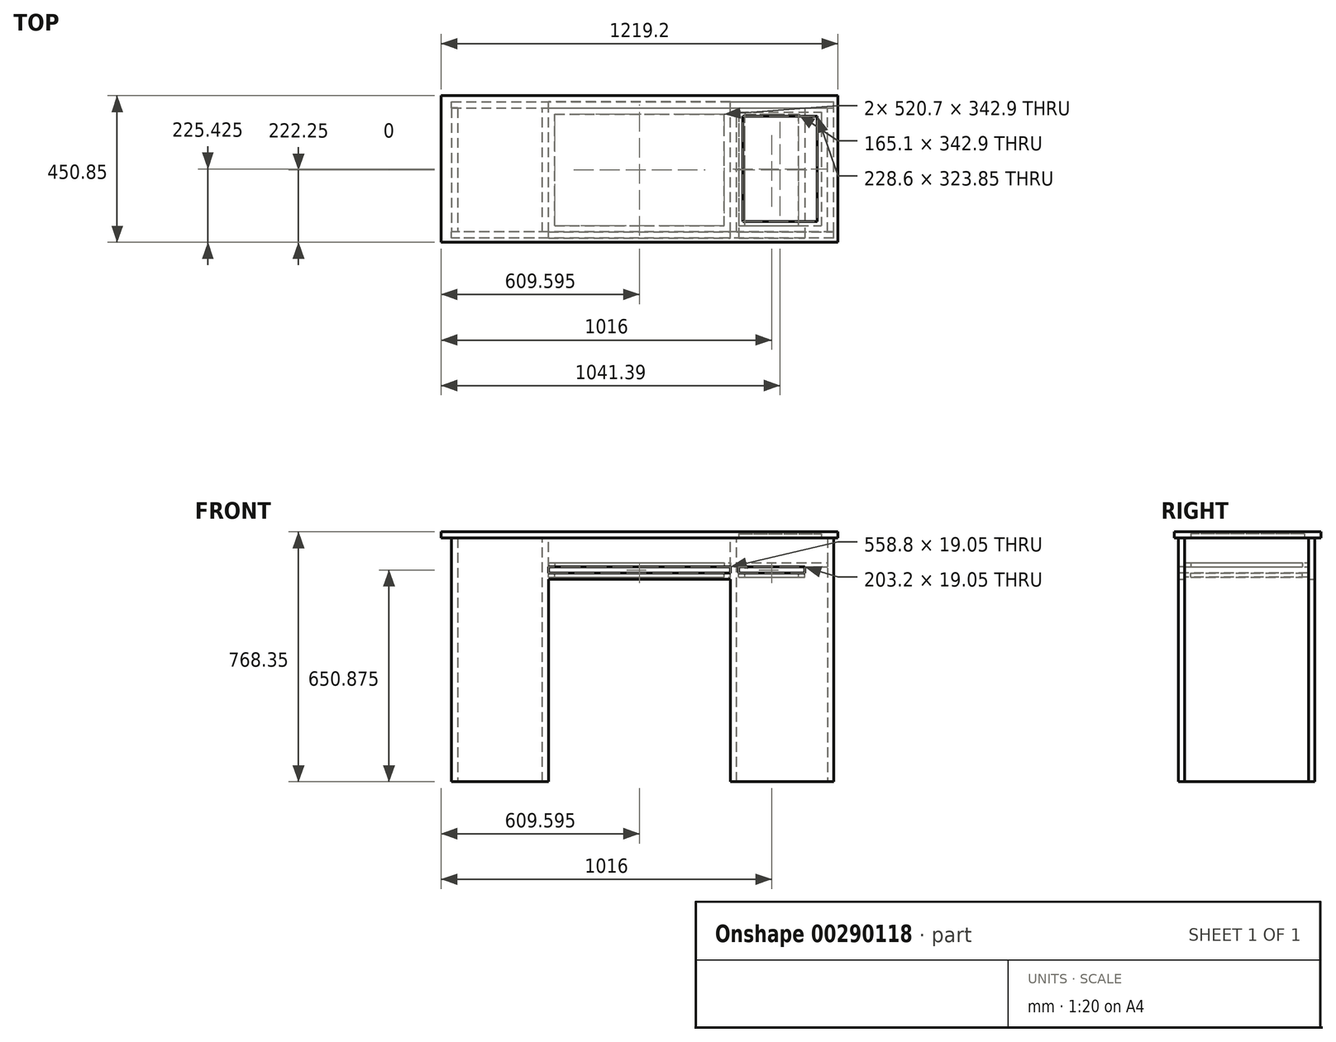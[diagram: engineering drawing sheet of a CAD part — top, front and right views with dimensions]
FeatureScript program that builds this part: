
annotation { "Feature Type Name" : "Feature", "Feature Type Description" : "" }
export const myFeature = defineFeature(function(context is Context, id is Id, definition is map)
    precondition{}
    {
        {
            var Q0;
            Q0=qCreatedBy(makeId("Front.planeOp"),FACE);
            var sketch = newSketch(context, id + "F0", { "sketchPlane" : qUnion([Q0])});
            skLineSegment(sketch, "E0.bottom", {"start": v(587.37, 374.65) * mm, "end": v(-587.38, 374.65) * mm});
            skLineSegment(sketch, "E0.top", {"start": v(587.38, -374.65) * mm, "end": v(269.87, -374.65) * mm});
            skLineSegment(sketch, "E0.left", {"start": v(587.38, 374.65) * mm, "end": v(587.38, -374.65) * mm});
            skLineSegment(sketch, "E0.right", {"start": v(-587.38, 374.65) * mm, "end": v(-587.38, -374.65) * mm});
            skPoint(sketch, "E0.middle", {"position": v(0, 0) * mm});
            skLineSegment(sketch, "E1", {"start": v(-288.93, -374.65) * mm, "end": v(-288.93, 247.65) * mm});
            skLineSegment(sketch, "E2", {"start": v(-288.93, 247.65) * mm, "end": v(269.87, 247.65) * mm});
            skLineSegment(sketch, "E3", {"start": v(269.87, 247.65) * mm, "end": v(269.87, -374.65) * mm});
            skLineSegment(sketch, "E4.trimOffspring", {"start": v(-288.93, -374.65) * mm, "end": v(-587.37, -374.65) * mm});
            skSolve(sketch);
        }
        {
            var Q0;
            Q0 = qSketchRegion(id + "F0", true);
            extrude(context, id + "F1", {"entities" : qUnion([Q0]), "depth" : 19.05 * mm});
        }
        {
            var Q0;
            Q0=makeQuery(id+"F1.opExtrude","SWEPT_FACE",FACE,{"disambiguationData":[OSD([sQuery(id+"F0.wireOp",EDGE,"E0.bottom")])]});
            var sketch = newSketch(context, id + "F2", { "sketchPlane" : qUnion([Q0])});
            skLineSegment(sketch, "E5.bottom", {"start": v(-619.13, -31.75) * mm, "end": v(600.07, -31.75) * mm});
            skLineSegment(sketch, "E5.top", {"start": v(-619.13, 419.1) * mm, "end": v(600.07, 419.1) * mm});
            skLineSegment(sketch, "E5.left", {"start": v(-619.13, -31.75) * mm, "end": v(-619.13, 419.1) * mm});
            skLineSegment(sketch, "E5.right", {"start": v(600.07, -31.75) * mm, "end": v(600.07, 419.1) * mm});
            skSolve(sketch);
        }
        {
            var Q0;
            Q0 = qSketchRegion(id + "F2", true);
            extrude(context, id + "F3", {"entities" : qUnion([Q0]), "operationType" : NewBodyOperationType.ADD, "depth" : 19.05 * mm});
        }
        {
            var Q0;
            Q0=qCreatedBy(makeId("Front.planeOp"),FACE);
            cPlane(context, id + "F4", {"entities" : qUnion([Q0]), "cplaneType" : CPlaneType.OFFSET, "offset" : 400.05 * mm, "oppositeDirection" : true, "width" : 152.4 * mm, "height" : 152.4 * mm});
        }
        {
            var Q0;
            Q0=qCreatedBy(id+"F4.planeOp",FACE);
            var sketch = newSketch(context, id + "F5", { "sketchPlane" : qUnion([Q0])});
            skLineSegment(sketch, "E6.bottom", {"start": v(-587.38, 374.65) * mm, "end": v(587.38, 374.65) * mm});
            skLineSegment(sketch, "E6.top", {"start": v(-587.38, -374.65) * mm, "end": v(-288.93, -374.65) * mm});
            skLineSegment(sketch, "E6.left", {"start": v(-587.38, 374.65) * mm, "end": v(-587.38, -374.65) * mm});
            skLineSegment(sketch, "E6.right", {"start": v(587.38, 374.65) * mm, "end": v(587.38, -374.65) * mm});
            skPoint(sketch, "E6.middle", {"position": v(0, 0) * mm});
            skLineSegment(sketch, "E7", {"start": v(269.87, -374.65) * mm, "end": v(269.87, 247.65) * mm});
            skLineSegment(sketch, "E8", {"start": v(269.87, 247.65) * mm, "end": v(-288.93, 247.65) * mm});
            skLineSegment(sketch, "E9", {"start": v(-288.93, 247.65) * mm, "end": v(-288.93, -374.65) * mm});
            skLineSegment(sketch, "E10.trimOffspring", {"start": v(269.87, -374.65) * mm, "end": v(587.38, -374.65) * mm});
            skSolve(sketch);
        }
        {
            var Q0;
            Q0 = qSketchRegion(id + "F5", true);
            extrude(context, id + "F6", {"entities" : qUnion([Q0]), "operationType" : NewBodyOperationType.ADD, "depth" : 19.05 * mm});
        }
        {
            var Q0;
            Q0=qCreatedBy(makeId("Right.planeOp"),FACE);
            cPlane(context, id + "F7", {"entities" : qUnion([Q0]), "cplaneType" : CPlaneType.OFFSET, "offset" : 587.68 * mm, "width" : 152.4 * mm, "height" : 152.4 * mm});
        }
        {
            var Q0;
            Q0=qCreatedBy(makeId("Right.planeOp"),FACE);
            cPlane(context, id + "F8", {"entities" : qUnion([Q0]), "cplaneType" : CPlaneType.OFFSET, "offset" : 587.68 * mm, "oppositeDirection" : true, "width" : 152.4 * mm, "height" : 152.4 * mm});
        }
        {
            var Q0;
            Q0=qCreatedBy(id+"F8.planeOp",FACE);
            var sketch = newSketch(context, id + "F9", { "sketchPlane" : qUnion([Q0])});
            skLineSegment(sketch, "E11.bottom", {"start": v(381, 374.65) * mm, "end": v(0, 374.65) * mm});
            skLineSegment(sketch, "E11.top", {"start": v(381, -374.65) * mm, "end": v(0, -374.65) * mm});
            skLineSegment(sketch, "E11.left", {"start": v(381, 374.65) * mm, "end": v(381, -374.65) * mm});
            skLineSegment(sketch, "E11.right", {"start": v(0, 374.65) * mm, "end": v(0, -374.65) * mm});
            skSolve(sketch);
        }
        {
            var Q0;
            Q0=makeQuery(id+"F9.imprint","IMPRINT",FACE,{"disambiguationData":[TD([[makeQuery(id+"F9.imprint","IMPRINT",EDGE,{"derivedFrom":sQuery(id+"F9.wireOp",EDGE,"E11.bottom")}),1.0]])]});
            extrude(context, id + "F10", {"entities" : qUnion([Q0]), "depth" : 19.05 * mm});
        }
        {
            var Q0;
            Q0=qCreatedBy(id+"F7.planeOp",FACE);
            var sketch = newSketch(context, id + "F11", { "sketchPlane" : qUnion([Q0])});
            skLineSegment(sketch, "E12.bottom", {"start": v(0, 374.65) * mm, "end": v(381, 374.65) * mm});
            skLineSegment(sketch, "E12.top", {"start": v(0, -374.65) * mm, "end": v(381, -374.65) * mm});
            skLineSegment(sketch, "E12.left", {"start": v(0, 374.65) * mm, "end": v(0, -374.65) * mm});
            skLineSegment(sketch, "E12.right", {"start": v(381, 374.65) * mm, "end": v(381, -374.65) * mm});
            skSolve(sketch);
        }
        {
            var Q0;
            Q0 = qSketchRegion(id + "F11", true);
            extrude(context, id + "F12", {"entities" : qUnion([Q0]), "oppositeDirection" : true, "depth" : 19.05 * mm});
        }
        {
            var Q0;
            Q0=makeQuery(id+"F1.opExtrude","CAP_FACE",FACE,{"disambiguationData":[OSD([sQuery(id+"F0.wireOp",EDGE,"E0.bottom"),sQuery(id+"F0.wireOp",EDGE,"E0.top"),sQuery(id+"F0.wireOp",EDGE,"E0.left"),sQuery(id+"F0.wireOp",EDGE,"E0.right"),sQuery(id+"F0.wireOp",EDGE,"E1"),sQuery(id+"F0.wireOp",EDGE,"E2"),sQuery(id+"F0.wireOp",EDGE,"E3"),sQuery(id+"F0.wireOp",EDGE,"E4.trimOffspring")])],"isStart":false});
            var sketch = newSketch(context, id + "F13", { "sketchPlane" : qUnion([Q0])});
            skLineSegment(sketch, "E13.bottom", {"start": v(-288.93, 285.75) * mm, "end": v(269.88, 285.75) * mm});
            skLineSegment(sketch, "E13.top", {"start": v(-288.93, 266.7) * mm, "end": v(269.88, 266.7) * mm});
            skLineSegment(sketch, "E13.left", {"start": v(-288.93, 285.75) * mm, "end": v(-288.93, 266.7) * mm});
            skLineSegment(sketch, "E13.right", {"start": v(269.88, 285.75) * mm, "end": v(269.88, 266.7) * mm});
            skSolve(sketch);
        }
        {
            var Q0;
            Q0=makeQuery(id+"F13.imprint","IMPRINT",FACE,{"disambiguationData":[TD([[makeQuery(id+"F13.imprint","IMPRINT",EDGE,{"derivedFrom":sQuery(id+"F13.wireOp",EDGE,"E13.bottom")}),-1.0]])]});
            extrude(context, id + "F14", {"entities" : qUnion([Q0]), "operationType" : NewBodyOperationType.REMOVE, "oppositeDirection" : true, "depth" : 19.05 * mm});
        }
        {
            var Q0;
            Q0=makeQuery(id+"F1.opExtrude","CAP_FACE",FACE,{"disambiguationData":[OSD([sQuery(id+"F0.wireOp",EDGE,"E0.bottom"),sQuery(id+"F0.wireOp",EDGE,"E0.top"),sQuery(id+"F0.wireOp",EDGE,"E0.left"),sQuery(id+"F0.wireOp",EDGE,"E0.right"),sQuery(id+"F0.wireOp",EDGE,"E1"),sQuery(id+"F0.wireOp",EDGE,"E2"),sQuery(id+"F0.wireOp",EDGE,"E3"),sQuery(id+"F0.wireOp",EDGE,"E4.trimOffspring")])],"isStart":false});
            var sketch = newSketch(context, id + "F15", { "sketchPlane" : qUnion([Q0])});
            skLineSegment(sketch, "E14.bottom", {"start": v(295.28, 266.7) * mm, "end": v(498.48, 266.7) * mm});
            skLineSegment(sketch, "E14.top", {"start": v(295.28, 285.75) * mm, "end": v(498.48, 285.75) * mm});
            skLineSegment(sketch, "E14.left", {"start": v(295.28, 266.7) * mm, "end": v(295.28, 285.75) * mm});
            skLineSegment(sketch, "E14.right", {"start": v(498.48, 266.7) * mm, "end": v(498.48, 285.75) * mm});
            skSolve(sketch);
        }
        {
            var Q0;
            Q0=makeQuery(id+"F15.imprint","IMPRINT",FACE,{"disambiguationData":[TD([[makeQuery(id+"F15.imprint","IMPRINT",EDGE,{"derivedFrom":sQuery(id+"F15.wireOp",EDGE,"E14.bottom")}),1.0]])]});
            extrude(context, id + "F16", {"entities" : qUnion([Q0]), "operationType" : NewBodyOperationType.REMOVE, "oppositeDirection" : true, "depth" : 19.05 * mm});
        }
        {
            var Q0;
            Q0=makeQuery(id+"F3.opExtrude","CAP_FACE",FACE,{"disambiguationData":[OSD([sQuery(id+"F2.wireOp",EDGE,"E5.bottom"),sQuery(id+"F2.wireOp",EDGE,"E5.top"),sQuery(id+"F2.wireOp",EDGE,"E5.left"),sQuery(id+"F2.wireOp",EDGE,"E5.right")])],"isStart":false});
            var sketch = newSketch(context, id + "F17", { "sketchPlane" : qUnion([Q0])});
            skLineSegment(sketch, "E15.bottom", {"start": v(307.97, 355.6) * mm, "end": v(536.57, 355.6) * mm});
            skLineSegment(sketch, "E15.top", {"start": v(307.97, 31.75) * mm, "end": v(536.57, 31.75) * mm});
            skLineSegment(sketch, "E15.left", {"start": v(307.97, 355.6) * mm, "end": v(307.97, 31.75) * mm});
            skLineSegment(sketch, "E15.right", {"start": v(536.57, 355.6) * mm, "end": v(536.57, 31.75) * mm});
            skSolve(sketch);
        }
        {
            var Q0;
            Q0=makeQuery(id+"F17.imprint","IMPRINT",FACE,{"disambiguationData":[TD([[makeQuery(id+"F17.imprint","IMPRINT",EDGE,{"derivedFrom":sQuery(id+"F17.wireOp",EDGE,"E15.bottom")}),-1.0]])]});
            extrude(context, id + "F18", {"entities" : qUnion([Q0]), "operationType" : NewBodyOperationType.REMOVE, "oppositeDirection" : true, "depth" : 19.05 * mm});
        }
        {
            var Q0;
            Q0=makeQuery(id+"F14.boolean.opBoolean","COPY",FACE,{"derivedFrom":makeQuery(id+"F14.opExtrude","SWEPT_FACE",FACE,{"disambiguationData":[OSD([sQuery(id+"F13.wireOp",EDGE,"E13.bottom")])]})});
            var sketch = newSketch(context, id + "F19", { "sketchPlane" : qUnion([Q0])});
            skLineSegment(sketch, "E16.top", {"start": v(-288.93, -381) * mm, "end": v(269.88, -381) * mm});
            skLineSegment(sketch, "E16.left", {"start": v(-288.93, 0) * mm, "end": v(-288.93, -381) * mm});
            skLineSegment(sketch, "E16.right", {"start": v(269.88, 0) * mm, "end": v(269.88, -381) * mm});
            skLineSegment(sketch, "E17", {"start": v(-269.88, -361.95) * mm, "end": v(250.83, -361.95) * mm});
            skLineSegment(sketch, "E18", {"start": v(-269.88, -19.05) * mm, "end": v(250.83, -19.05) * mm});
            skPoint(sketch, "E19.trimOffspring.start.orphan", {"position": v(253.1, 0) * mm});
            skLineSegment(sketch, "E20", {"start": v(-288.93, 0) * mm, "end": v(269.88, 0) * mm});
            skPoint(sketch, "E21.end.orphan", {"position": v(253.1, -171.45) * mm});
            skLineSegment(sketch, "E22", {"start": v(-269.88, -19.05) * mm, "end": v(-269.88, -361.95) * mm});
            skLineSegment(sketch, "E23", {"start": v(250.83, -19.05) * mm, "end": v(250.83, -361.95) * mm});
            skLineSegment(sketch, "E24.bottom", {"start": v(288.93, 0) * mm, "end": v(568.63, 0) * mm});
            skLineSegment(sketch, "E24.top", {"start": v(288.93, -381) * mm, "end": v(568.63, -381) * mm});
            skLineSegment(sketch, "E24.left", {"start": v(288.93, 0) * mm, "end": v(288.93, -381) * mm});
            skLineSegment(sketch, "E24.right", {"start": v(568.63, 0) * mm, "end": v(568.63, -381) * mm});
            skSolve(sketch);
        }
        {
            var Q0;
            Q0 = qSketchRegion(id + "F19", true);
            extrude(context, id + "F20", {"entities" : qUnion([Q0]), "oppositeDirection" : true, "depth" : 12.7 * mm});
        }
        {
            var Q0;
            Q0=makeQuery(id+"F14.boolean.opBoolean","COPY",FACE,{"derivedFrom":makeQuery(id+"F14.opExtrude","SWEPT_FACE",FACE,{"disambiguationData":[OSD([sQuery(id+"F13.wireOp",EDGE,"E13.top")])]})});
            var sketch = newSketch(context, id + "F21", { "sketchPlane" : qUnion([Q0])});
            skLineSegment(sketch, "E25.top", {"start": v(-288.93, 0) * mm, "end": v(269.88, 0) * mm});
            skLineSegment(sketch, "E25.left", {"start": v(-288.93, 381) * mm, "end": v(-288.93, 0) * mm});
            skLineSegment(sketch, "E25.right", {"start": v(269.88, 381) * mm, "end": v(269.88, 0) * mm});
            skLineSegment(sketch, "E26", {"start": v(-269.88, 19.05) * mm, "end": v(250.83, 19.05) * mm});
            skLineSegment(sketch, "E27.top", {"start": v(295.28, 0) * mm, "end": v(498.48, 0) * mm});
            skLineSegment(sketch, "E27.left", {"start": v(295.28, 381) * mm, "end": v(295.28, 0) * mm});
            skLineSegment(sketch, "E27.right", {"start": v(498.48, 381) * mm, "end": v(498.48, 0) * mm});
            skLineSegment(sketch, "E28", {"start": v(314.33, 19.05) * mm, "end": v(479.43, 19.05) * mm});
            skLineSegment(sketch, "E29", {"start": v(-269.88, 361.95) * mm, "end": v(250.82, 361.95) * mm});
            skPoint(sketch, "E30.trimOffspring.start.orphan", {"position": v(253.1, 381) * mm});
            skLineSegment(sketch, "E31", {"start": v(-288.93, 381) * mm, "end": v(269.88, 381) * mm});
            skLineSegment(sketch, "E32", {"start": v(314.33, 361.95) * mm, "end": v(479.42, 361.95) * mm});
            skPoint(sketch, "E33.orphan", {"position": v(481.7, 381) * mm});
            skLineSegment(sketch, "E34", {"start": v(295.28, 381) * mm, "end": v(498.48, 381) * mm});
            skPoint(sketch, "E35.end.orphan", {"position": v(253.1, 209.55) * mm});
            skPoint(sketch, "E36.start.orphan", {"position": v(316.6, 209.55) * mm});
            skLineSegment(sketch, "E37", {"start": v(-269.88, 19.05) * mm, "end": v(-269.88, 361.95) * mm});
            skLineSegment(sketch, "E38", {"start": v(250.83, 19.05) * mm, "end": v(250.82, 361.95) * mm});
            skLineSegment(sketch, "E39", {"start": v(314.33, 19.05) * mm, "end": v(314.33, 361.95) * mm});
            skLineSegment(sketch, "E40", {"start": v(479.43, 19.05) * mm, "end": v(479.42, 361.95) * mm});
            skSolve(sketch);
        }
        {
            var Q0;
            Q0 = qSketchRegion(id + "F21", true);
            extrude(context, id + "F22", {"entities" : qUnion([Q0]), "oppositeDirection" : true, "depth" : 12.7 * mm});
        }
        {
            var Q0;
            Q0=makeQuery(id+"F12.boolean.opBoolean","SPLIT",FACE,{"disambiguationData":[TD([makeQuery(id+"F10.opExtrude","CAP_FACE",FACE,{"disambiguationData":[OSD([sQuery(id+"F9.wireOp",EDGE,"E11.bottom"),sQuery(id+"F9.wireOp",EDGE,"E11.top"),sQuery(id+"F9.wireOp",EDGE,"E11.left"),sQuery(id+"F9.wireOp",EDGE,"E11.right")])],"isStart":false})])],"derivedFrom":makeQuery(id+"F3.opExtrude","CAP_FACE",FACE,{"disambiguationData":[OSD([sQuery(id+"F2.wireOp",EDGE,"E5.bottom"),sQuery(id+"F2.wireOp",EDGE,"E5.top"),sQuery(id+"F2.wireOp",EDGE,"E5.left"),sQuery(id+"F2.wireOp",EDGE,"E5.right")])],"isStart":true})});
            var sketch = newSketch(context, id + "F23", { "sketchPlane" : qUnion([Q0])});
            skLineSegment(sketch, "E41.bottom", {"start": v(-307.98, 0) * mm, "end": v(-288.93, 0) * mm});
            skLineSegment(sketch, "E41.top", {"start": v(-307.98, -381) * mm, "end": v(-288.93, -381) * mm});
            skLineSegment(sketch, "E41.left", {"start": v(-307.98, 0) * mm, "end": v(-307.98, -381) * mm});
            skLineSegment(sketch, "E41.right", {"start": v(-288.93, 0) * mm, "end": v(-288.93, -381) * mm});
            skLineSegment(sketch, "E42.bottom", {"start": v(269.88, 0) * mm, "end": v(288.93, 0) * mm});
            skLineSegment(sketch, "E42.top", {"start": v(269.88, -381) * mm, "end": v(288.93, -381) * mm});
            skLineSegment(sketch, "E42.left", {"start": v(269.88, 0) * mm, "end": v(269.88, -381) * mm});
            skLineSegment(sketch, "E42.right", {"start": v(288.93, 0) * mm, "end": v(288.93, -381) * mm});
            skSolve(sketch);
        }
        {
            var Q0;
            Q0 = qSketchRegion(id + "F23", true);
            extrude(context, id + "F24", {"entities" : qUnion([Q0]), "depth" : 749.3 * mm});
        }
        {
            var Q0;
            Q0=makeQuery(id+"F3.opExtrude","CAP_FACE",FACE,{"disambiguationData":[OSD([sQuery(id+"F2.wireOp",EDGE,"E5.bottom"),sQuery(id+"F2.wireOp",EDGE,"E5.top"),sQuery(id+"F2.wireOp",EDGE,"E5.left"),sQuery(id+"F2.wireOp",EDGE,"E5.right")])],"isStart":true});
            var sketch = newSketch(context, id + "F25", { "sketchPlane" : qUnion([Q0])});
            skLineSegment(sketch, "E43.bottom", {"start": v(295.27, -368.3) * mm, "end": v(549.27, -368.3) * mm});
            skLineSegment(sketch, "E43.top", {"start": v(295.27, -19.05) * mm, "end": v(549.27, -19.05) * mm});
            skLineSegment(sketch, "E43.left", {"start": v(295.27, -368.3) * mm, "end": v(295.27, -19.05) * mm});
            skLineSegment(sketch, "E43.right", {"start": v(549.27, -368.3) * mm, "end": v(549.27, -19.05) * mm});
            skSolve(sketch);
        }
        {
            var Q0;
            Q0 = qSketchRegion(id + "F25", true);
            extrude(context, id + "F26", {"entities" : qUnion([Q0]), "operationType" : NewBodyOperationType.REMOVE, "oppositeDirection" : true, "depth" : 12.7 * mm});
        }
    });
